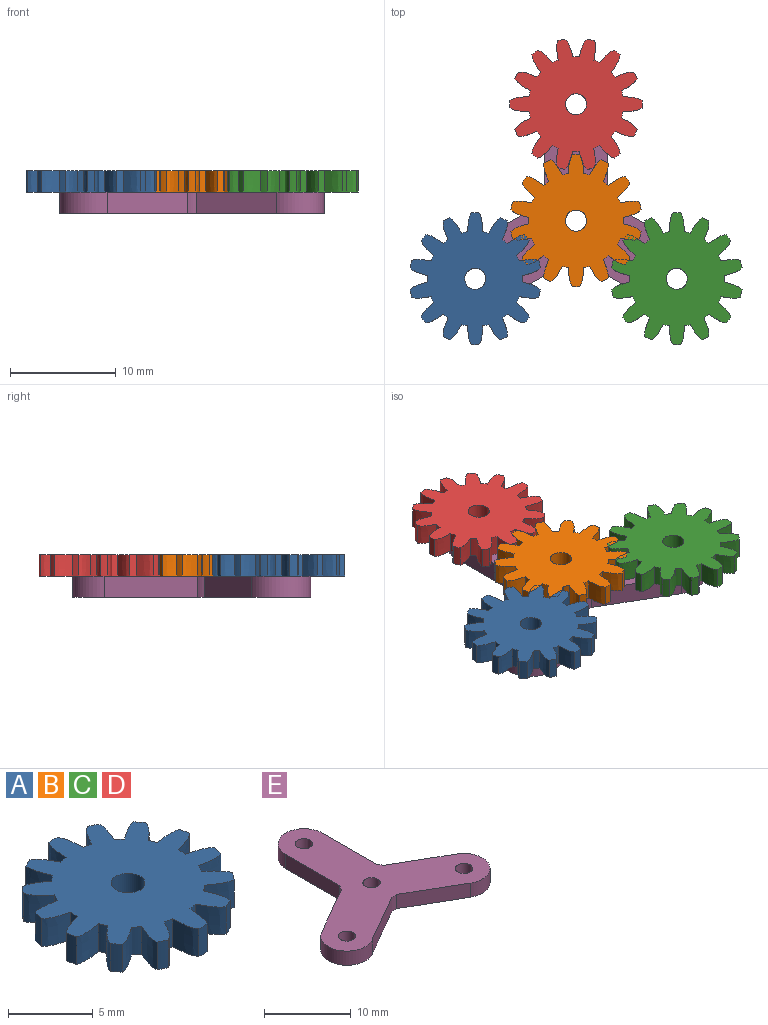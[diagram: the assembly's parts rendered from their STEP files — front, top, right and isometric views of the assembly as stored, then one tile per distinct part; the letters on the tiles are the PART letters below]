
ASSEMBLY  parts=5 mates=4
PART A: 59 faces, bbox 12.3x12.5x2 mm
  f0: cylinder r=4.5mm len=2mm, axis (0,0,-1), area 1.2mm2, adj f18,f19,f40,f43
  f1: cylinder r=4.5mm len=2mm, axis (0,0,-1), area 1.2mm2, adj f13,f18,f19,f42
  f2: cylinder r=4.5mm len=2mm, axis (0,0,-1), area 1.2mm2, adj f18,f19,f37,f39
  f3: cylinder r=4.5mm len=2mm, axis (0,0,-1), area 1.2mm2, adj f18,f19,f34,f36
  f4: cylinder r=4.5mm len=2mm, axis (0,0,-1), area 1.2mm2, adj f18,f19,f31,f33
  f5: cylinder r=4.5mm len=2mm, axis (0,0,-1), area 1.2mm2, adj f18,f19,f28,f30
  f6: cylinder r=4.5mm len=2mm, axis (0,0,-1), area 1.2mm2, adj f18,f19,f25,f27
  f7: cylinder r=4.5mm len=2mm, axis (0,0,-1), area 1.2mm2, adj f18,f19,f22,f24
  f8: cylinder r=4.5mm len=2mm, axis (0,0,-1), area 1.2mm2, adj f18,f19,f21,f57
  f9: cylinder r=4.5mm len=2mm, axis (0,0,-1), area 1.2mm2, adj f18,f19,f55,f56
  f10: cylinder r=4.5mm len=2mm, axis (0,0,-1), area 1.2mm2, adj f18,f19,f52,f54
  f11: cylinder r=4.5mm len=2mm, axis (0,0,-1), area 1.2mm2, adj f18,f19,f49,f51
  f12: cylinder r=4.5mm len=2mm, axis (0,0,-1), area 1.2mm2, adj f18,f19,f45,f48
  f13: extruded ~2x1.41mm, area 3.7mm2, adj f1,f16,f18,f19
  f14: cylinder r=4.5mm len=2mm, axis (0,0,-1), area 1.2mm2, adj f15,f18,f19,f46
  f15: extruded ~2x1.63mm, area 3.7mm2, adj f14,f16,f18,f19
  f16: cylinder r=6.25mm len=2mm, axis (0,0,-1), area 1.4mm2, adj f13,f15,f18,f19
  f17: cylinder r=1mm len=2mm, axis (0,0,-1), area 12.6mm2, adj f18,f19
  f18: plane 12.5x12.32mm, normal (0,0,1), area 90.6mm2, adj f0,f1,f2,f3,f4,f5,f6,f7
  f19: plane 12.5x12.32mm, normal (0,0,-1), area 90.6mm2, adj f0,f1,f2,f3,f4,f5,f6,f7
  f20: cylinder r=6.25mm len=2mm, axis (0,0,-1), area 1.4mm2, adj f18,f19,f21,f22
  f21: extruded ~2x1.67mm, area 3.7mm2, adj f8,f18,f19,f20
  f22: extruded ~2x1.83mm, area 3.7mm2, adj f7,f18,f19,f20
  f23: cylinder r=6.25mm len=2mm, axis (0,0,-1), area 1.4mm2, adj f18,f19,f24,f25
  f24: extruded ~2x1.41mm, area 3.7mm2, adj f7,f18,f19,f23
  f25: extruded ~2x1.63mm, area 3.7mm2, adj f6,f18,f19,f23
  f26: cylinder r=6.25mm len=2mm, axis (0,0,-1), area 1.4mm2, adj f18,f19,f27,f28
  f27: extruded ~2x1.78mm, area 3.7mm2, adj f6,f18,f19,f26
  f28: extruded ~2x1.46mm, area 3.7mm2, adj f5,f18,f19,f26
  f29: cylinder r=6.25mm len=2mm, axis (0,0,-1), area 1.4mm2, adj f18,f19,f30,f31
  f30: extruded ~2x1.8mm, area 3.7mm2, adj f5,f18,f19,f29
  f31: extruded ~2x1.8mm, area 3.7mm2, adj f4,f18,f19,f29
  f32: cylinder r=6.25mm len=2mm, axis (0,0,-1), area 1.4mm2, adj f18,f19,f33,f34
  f33: extruded ~2x1.46mm, area 3.7mm2, adj f4,f18,f19,f32
  f34: extruded ~2x1.78mm, area 3.7mm2, adj f3,f18,f19,f32
  f35: cylinder r=6.25mm len=2mm, axis (0,0,-1), area 1.4mm2, adj f18,f19,f36,f37
  f36: extruded ~2x1.63mm, area 3.7mm2, adj f3,f18,f19,f35
  f37: extruded ~2x1.41mm, area 3.7mm2, adj f2,f18,f19,f35
  f38: cylinder r=6.25mm len=2mm, axis (0,0,-1), area 1.4mm2, adj f18,f19,f39,f40
  f39: extruded ~2x1.83mm, area 3.7mm2, adj f2,f18,f19,f38
  f40: extruded ~2x1.67mm, area 3.7mm2, adj f0,f18,f19,f38
  f41: cylinder r=6.25mm len=2mm, axis (0,0,-1), area 1.4mm2, adj f18,f19,f42,f43
  f42: extruded ~2x1.83mm, area 3.7mm2, adj f1,f18,f19,f41
  f43: extruded ~2x1.67mm, area 3.7mm2, adj f0,f18,f19,f41
  f44: cylinder r=6.25mm len=2mm, axis (0,0,-1), area 1.4mm2, adj f18,f19,f45,f46
  f45: extruded ~2x1.46mm, area 3.7mm2, adj f12,f18,f19,f44
  f46: extruded ~2x1.78mm, area 3.7mm2, adj f14,f18,f19,f44
  f47: cylinder r=6.25mm len=2mm, axis (0,0,-1), area 1.4mm2, adj f18,f19,f48,f49
  f48: extruded ~2x1.8mm, area 3.7mm2, adj f12,f18,f19,f47
  f49: extruded ~2x1.8mm, area 3.7mm2, adj f11,f18,f19,f47
  f50: cylinder r=6.25mm len=2mm, axis (0,0,-1), area 1.4mm2, adj f18,f19,f51,f52
  f51: extruded ~2x1.46mm, area 3.7mm2, adj f11,f18,f19,f50
  f52: extruded ~2x1.78mm, area 3.7mm2, adj f10,f18,f19,f50
  f53: cylinder r=6.25mm len=2mm, axis (0,0,-1), area 1.4mm2, adj f18,f19,f54,f55
  f54: extruded ~2x1.63mm, area 3.7mm2, adj f10,f18,f19,f53
  f55: extruded ~2x1.41mm, area 3.7mm2, adj f9,f18,f19,f53
  f56: extruded ~2x1.83mm, area 3.7mm2, adj f9,f18,f19,f58
  f57: extruded ~2x1.67mm, area 3.7mm2, adj f8,f18,f19,f58
  f58: cylinder r=6.25mm len=2mm, axis (0,0,-1), area 1.4mm2, adj f18,f19,f56,f57
PART B: same geometry as A
PART C: same geometry as A
PART D: same geometry as A
PART E: 18 faces, bbox 25.1x22.5x2 mm
  f0: cylinder r=3.72mm len=2mm, axis (0,0,-1), area 1.6mm2, adj f5,f8,f9,f14
  f1: cylinder r=3.72mm len=2mm, axis (0,0,-1), area 1.6mm2, adj f8,f9,f12,f16
  f2: cylinder r=3.72mm len=2mm, axis (0,0,-1), area 1.6mm2, adj f3,f8,f9,f13
  f3: plane 8.8x2mm, normal (1,0,0), area 17.6mm2, adj f2,f4,f8,f9
  f4: cylinder r=3mm len=6mm, axis (0,0,-1), area 18.8mm2, adj f3,f5,f8,f9
  f5: plane 8.8x2mm, normal (-1,0,0), area 17.6mm2, adj f0,f4,f8,f9
  f6: cylinder r=1mm len=2mm, axis (0,0,-1), area 12.6mm2, adj f8,f9
  f7: cylinder r=1mm len=2mm, axis (0,0,-1), area 12.6mm2, adj f8,f9
  f8: plane 25.05x22.5mm, normal (0,0,1), area 212.6mm2, adj f0,f1,f2,f3,f4,f5,f6,f7
  f9: plane 25.05x22.5mm, normal (0,0,-1), area 212.6mm2, adj f0,f1,f2,f3,f4,f5,f6,f7
  f10: cylinder r=3mm len=5.6mm, axis (0,0,-1), area 18.8mm2, adj f8,f9,f12,f13
  f11: cylinder r=1mm len=2mm, axis (0,0,-1), area 12.6mm2, adj f8,f9
  f12: plane 7.62x4.4mm, normal (-0.5,-0.87,0), area 17.6mm2, adj f1,f8,f9,f10
  f13: plane 7.62x4.4mm, normal (0.5,0.87,0), area 17.6mm2, adj f2,f8,f9,f10
  f14: plane 7.62x4.4mm, normal (-0.5,0.87,0), area 17.6mm2, adj f0,f8,f9,f15
  f15: cylinder r=3mm len=5.6mm, axis (0,0,-1), area 18.8mm2, adj f8,f9,f14,f16
  f16: plane 7.62x4.4mm, normal (0.5,-0.87,0), area 17.6mm2, adj f1,f8,f9,f15
  f17: cylinder r=1mm len=2mm, axis (0,0,-1), area 12.6mm2, adj f8,f9
PLACE A rot(axis=(1,0,0),180deg) t=(5.47,9.5,4)mm
PLACE B rot(axis=(1,0,0),180deg) t=(15,15,4)mm
PLACE C rot(axis=(1,0,0),180deg) t=(24.53,9.5,4)mm
PLACE D rot(axis=(0,0,-1),12.9deg) t=(15,26,2)mm
PLACE E at identity
MATE revolute C.f17 <-> E.f10  axis (0,0,-1) through (24.53,9.5,2)mm
MATE revolute B.f17 <-> E.f0  axis (0,0,-1) through (15,15,2)mm
MATE revolute D.f17 <-> E.f4  axis (0,0,-1) through (15,26,2)mm
MATE revolute A.f17 <-> E.f15  axis (0,0,-1) through (5.47,9.5,2)mm
